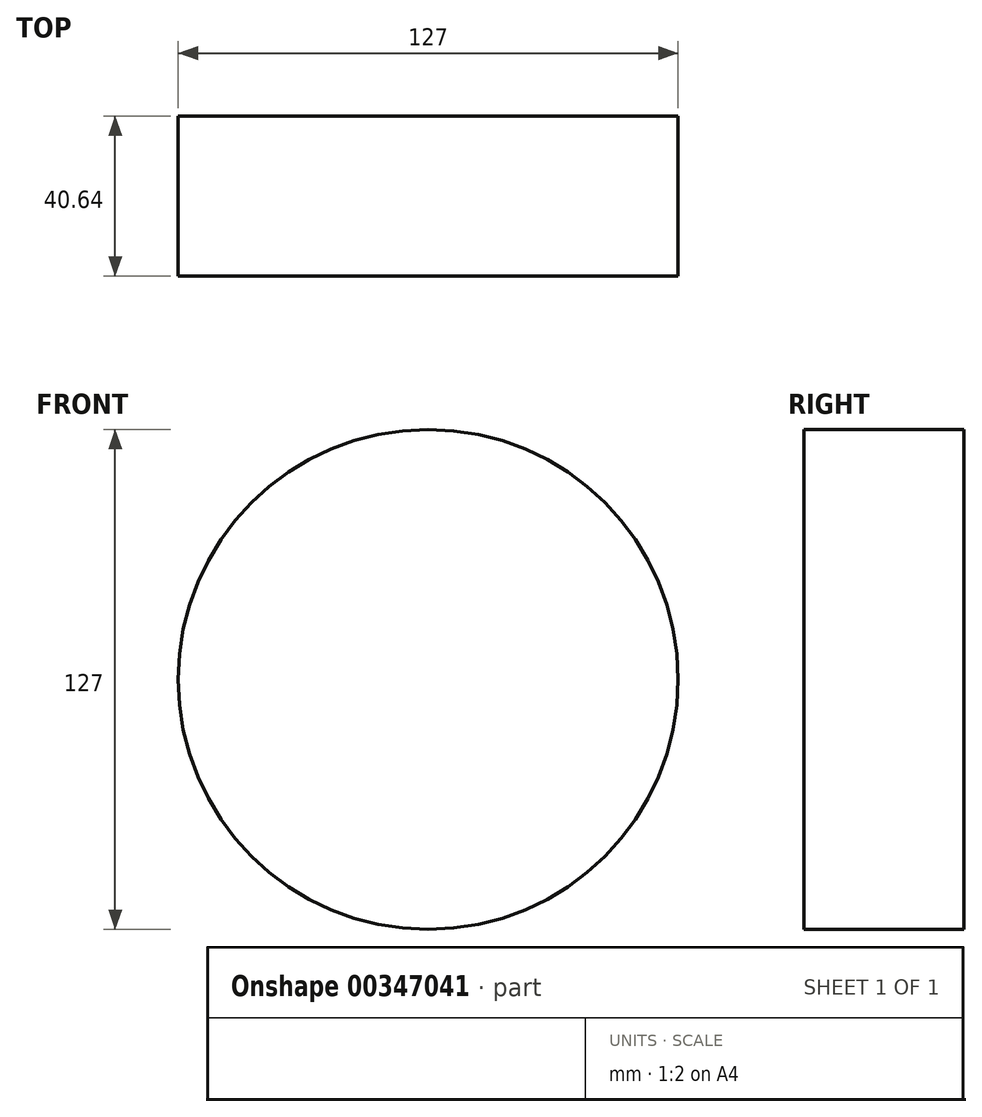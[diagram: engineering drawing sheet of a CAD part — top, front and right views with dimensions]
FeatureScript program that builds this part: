
annotation { "Feature Type Name" : "Feature", "Feature Type Description" : "" }
export const myFeature = defineFeature(function(context is Context, id is Id, definition is map)
    precondition{}
    {
        {
            var Q0;
            Q0=qCreatedBy(makeId("Front.planeOp"),FACE);
            var sketch = newSketch(context, id + "F0", { "sketchPlane" : qUnion([Q0])});
            skCircle(sketch, "E0", {"center": v(-63.03, 57.31) * mm, "radius": 63.5 * mm});
            skSolve(sketch);
        }
        {
            var Q0;
            Q0 = qSketchRegion(id + "F0", true);
            extrude(context, id + "F1", {"entities" : qUnion([Q0]), "depth" : 40.64 * mm, "offsetDistance" : 25.4 * mm});
        }
    });
